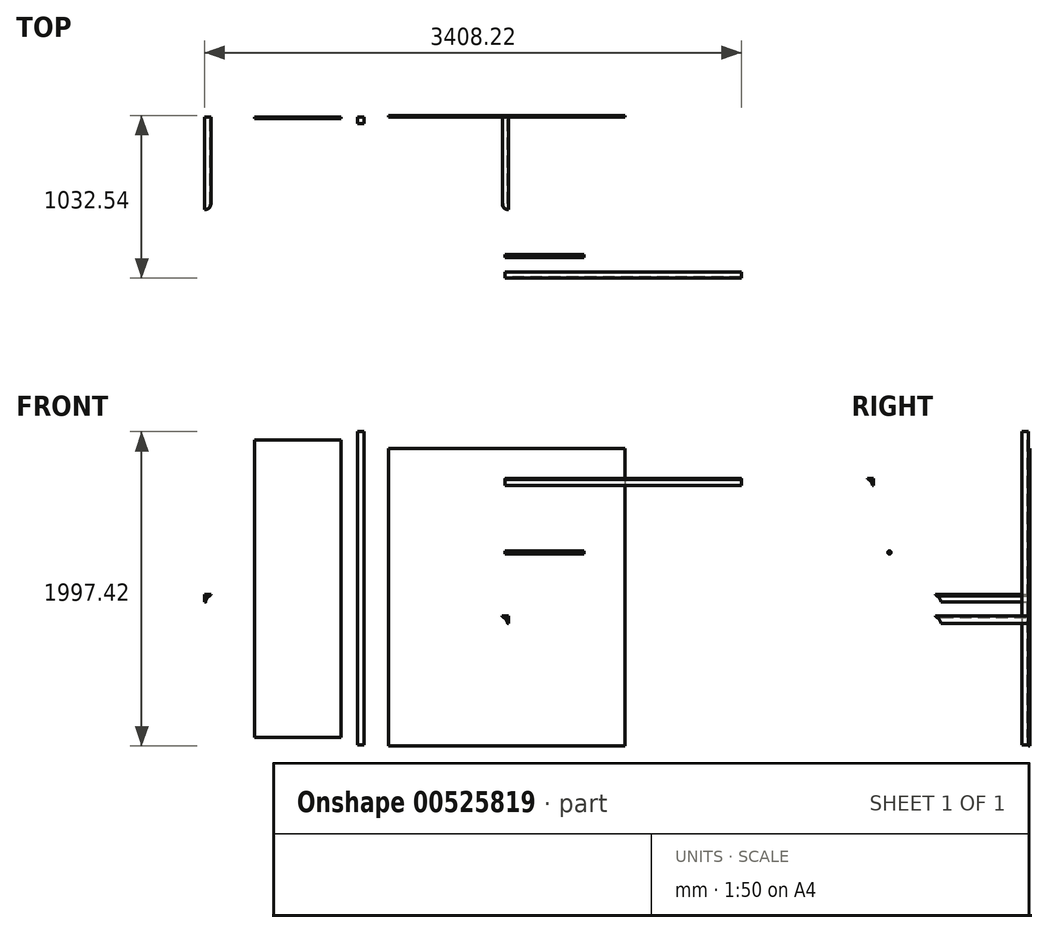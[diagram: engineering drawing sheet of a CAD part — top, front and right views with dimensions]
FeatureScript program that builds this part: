
annotation { "Feature Type Name" : "Feature", "Feature Type Description" : "" }
export const myFeature = defineFeature(function(context is Context, id is Id, definition is map)
    precondition{}
    {
        {
            var Q0;
            Q0=qCreatedBy(makeId("Front.planeOp"),FACE);
            var sketch = newSketch(context, id + "F0", { "sketchPlane" : qUnion([Q0])});
            skLineSegment(sketch, "E0.bottom", {"start": v(-740.02, 1080.66) * mm, "end": v(759.98, 1080.66) * mm});
            skLineSegment(sketch, "E0.top", {"start": v(-740.02, -809.34) * mm, "end": v(759.98, -809.34) * mm});
            skLineSegment(sketch, "E0.left", {"start": v(-740.02, 1080.66) * mm, "end": v(-740.02, -809.34) * mm});
            skLineSegment(sketch, "E0.right", {"start": v(759.98, 1080.66) * mm, "end": v(759.98, -809.34) * mm});
            skSolve(sketch);
        }
        {
            var Q0;
            Q0=makeQuery(id+"F0.imprint","IMPRINT",FACE,{"disambiguationData":[TD([[makeQuery(id+"F0.imprint","IMPRINT",EDGE,{"derivedFrom":sQuery(id+"F0.wireOp",EDGE,"E0.bottom")}),-1.0]])]});
            extrude(context, id + "F1", {"entities" : qUnion([Q0]), "depth" : 10 * mm, "offsetDistance" : 25 * mm});
        }
        {
            var Q0;
            Q0=makeQuery(id+"F1.opExtrude","CAP_FACE",FACE,{"disambiguationData":[OSD([sQuery(id+"F0.wireOp",EDGE,"E0.bottom"),sQuery(id+"F0.wireOp",EDGE,"E0.top"),sQuery(id+"F0.wireOp",EDGE,"E0.left"),sQuery(id+"F0.wireOp",EDGE,"E0.right")])],"isStart":false});
            var sketch = newSketch(context, id + "F2", { "sketchPlane" : qUnion([Q0])});
            skLineSegment(sketch, "E1.bottom", {"start": v(-937.53, 1188.08) * mm, "end": v(-897.53, 1188.08) * mm});
            skLineSegment(sketch, "E1.top", {"start": v(-937.53, -801.92) * mm, "end": v(-897.53, -801.92) * mm});
            skLineSegment(sketch, "E1.left", {"start": v(-937.53, 1188.08) * mm, "end": v(-937.53, -801.92) * mm});
            skLineSegment(sketch, "E1.right", {"start": v(-897.53, 1188.08) * mm, "end": v(-897.53, -801.92) * mm});
            skSolve(sketch);
        }
        {
            var Q0;
            Q0=makeQuery(id+"F2.imprint","IMPRINT",FACE,{"disambiguationData":[TD([[makeQuery(id+"F2.imprint","IMPRINT",EDGE,{"derivedFrom":sQuery(id+"F2.wireOp",EDGE,"E1.bottom")}),-1.0]])]});
            extrude(context, id + "F3", {"entities" : qUnion([Q0]), "depth" : 40 * mm, "offsetDistance" : 25 * mm});
        }
        {
            var Q0;
            Q0=makeQuery(id+"F1.opExtrude","CAP_FACE",FACE,{"disambiguationData":[OSD([sQuery(id+"F0.wireOp",EDGE,"E0.bottom"),sQuery(id+"F0.wireOp",EDGE,"E0.top"),sQuery(id+"F0.wireOp",EDGE,"E0.left"),sQuery(id+"F0.wireOp",EDGE,"E0.right")])],"isStart":false});
            var sketch = newSketch(context, id + "F4", { "sketchPlane" : qUnion([Q0])});
            skLineSegment(sketch, "E2.bottom", {"start": v(-1591.53, 1135.97) * mm, "end": v(-1041.53, 1135.97) * mm});
            skLineSegment(sketch, "E2.top", {"start": v(-1591.53, -754.03) * mm, "end": v(-1041.53, -754.03) * mm});
            skLineSegment(sketch, "E2.left", {"start": v(-1591.53, 1135.97) * mm, "end": v(-1591.53, -754.03) * mm});
            skLineSegment(sketch, "E2.right", {"start": v(-1041.53, 1135.97) * mm, "end": v(-1041.53, -754.03) * mm});
            skSolve(sketch);
        }
        {
            var Q0;
            Q0=makeQuery(id+"F4.imprint","IMPRINT",FACE,{"disambiguationData":[TD([[makeQuery(id+"F4.imprint","IMPRINT",EDGE,{"derivedFrom":sQuery(id+"F4.wireOp",EDGE,"E2.bottom")}),-1.0]])]});
            extrude(context, id + "F5", {"entities" : qUnion([Q0]), "depth" : 10 * mm, "offsetDistance" : 25 * mm});
        }
        {
            var Q0;
            Q0=qCreatedBy(makeId("Right.planeOp"),FACE);
            var sketch = newSketch(context, id + "F6", { "sketchPlane" : qUnion([Q0])});
            skCircle(sketch, "E3", {"center": v(-892.2, 420.17) * mm, "radius": 10 * mm});
            skSolve(sketch);
        }
        {
            var Q0;
            Q0=makeQuery(id+"F6.imprint","IMPRINT",FACE,{"disambiguationData":[TD([[makeQuery(id+"F6.imprint","IMPRINT",EDGE,{"derivedFrom":sQuery(id+"F6.wireOp",EDGE,"E3")}),1.0]])]});
            extrude(context, id + "F7", {"entities" : qUnion([Q0]), "depth" : 500 * mm, "offsetDistance" : 25 * mm});
        }
        {
            var Q0;
            Q0=makeQuery(id+"F1.opExtrude","CAP_FACE",FACE,{"disambiguationData":[OSD([sQuery(id+"F0.wireOp",EDGE,"E0.bottom"),sQuery(id+"F0.wireOp",EDGE,"E0.top"),sQuery(id+"F0.wireOp",EDGE,"E0.left"),sQuery(id+"F0.wireOp",EDGE,"E0.right")])],"isStart":false});
            var sketch = newSketch(context, id + "F8", { "sketchPlane" : qUnion([Q0])});
            skArc(sketch, "E4", {"start": v(-1875.7, 145) * mm, "mid": v(-1894.46, 128.87) * mm, "end": v(-1902.5, 105.47) * mm});
            skLineSegment(sketch, "E5", {"start": v(-1875.7, 145) * mm, "end": v(-1875.7, 149.02) * mm});
            skLineSegment(sketch, "E6", {"start": v(-1875.7, 149.02) * mm, "end": v(-1872.5, 149.02) * mm});
            skArc(sketch, "E7", {"start": v(-1872.5, 149.02) * mm, "mid": v(-1870, 150.17) * mm, "end": v(-1869.26, 152.8) * mm});
            skLineSegment(sketch, "E8", {"start": v(-1869.26, 152.8) * mm, "end": v(-1908.95, 152.8) * mm});
            skLineSegment(sketch, "E9", {"start": v(-1902.5, 105.47) * mm, "end": v(-1908.22, 105.47) * mm});
            skLineSegment(sketch, "E10", {"start": v(-1908.22, 105.47) * mm, "end": v(-1908.22, 152.8) * mm});
            skSolve(sketch);
        }
        {
            var Q0;
            Q0=makeQuery(id+"F8.imprint","IMPRINT",FACE,{"disambiguationData":[TD([[makeQuery(id+"F8.imprint","IMPRINT",EDGE,{"derivedFrom":sQuery(id+"F8.wireOp",EDGE,"E4")}),-1.0]])]});
            extrude(context, id + "F9", {"entities" : qUnion([Q0]), "depth" : 550 * mm, "offsetDistance" : 25 * mm});
        }
        {
            var Q0;
            Q0=makeQuery(id+"F9.opExtrude","CAP_FACE",FACE,{"disambiguationData":[OSD([sQuery(id+"F8.wireOp",EDGE,"E4"),sQuery(id+"F8.wireOp",EDGE,"E5"),sQuery(id+"F8.wireOp",EDGE,"E6"),sQuery(id+"F8.wireOp",EDGE,"E7"),sQuery(id+"F8.wireOp",EDGE,"E8"),sQuery(id+"F8.wireOp",EDGE,"E9"),sQuery(id+"F8.wireOp",EDGE,"E10")])],"isStart":false});
            var Q1;
            Q1=makeQuery(id+"F9.opExtrude","CAP_EDGE",EDGE,{"disambiguationData":[OSD([sQuery(id+"F8.wireOp",EDGE,"E10")])],"isStart":false});
            revolve(context, id + "F10", {"operationType" : NewBodyOperationType.ADD, "entities" : qUnion([Q0]), "axis" : qUnion([Q1]), "revolveType" : RevolveType.ONE_DIRECTION, "oppositeDirection" : true, "angle" : 90 * degree});
        }
        {
            var Q0;
            Q0=makeQuery(id+"F1.opExtrude","CAP_FACE",FACE,{"disambiguationData":[OSD([sQuery(id+"F0.wireOp",EDGE,"E0.bottom"),sQuery(id+"F0.wireOp",EDGE,"E0.top"),sQuery(id+"F0.wireOp",EDGE,"E0.left"),sQuery(id+"F0.wireOp",EDGE,"E0.right")])],"isStart":false});
            var sketch = newSketch(context, id + "F11", { "sketchPlane" : qUnion([Q0])});
            skLineSegment(sketch, "E11.MirrorCS", {"start": v(-12.22, 11.67) * mm, "end": v(-15.43, 11.67) * mm});
            skLineSegment(sketch, "E12.MirrorCS", {"start": v(-12.22, 7.63) * mm, "end": v(-12.22, 11.67) * mm});
            skArc(sketch, "E13.MirrorCS", {"start": v(-15.43, 11.67) * mm, "mid": v(-17.91, 12.8) * mm, "end": v(-18.66, 15.44) * mm});
            skLineSegment(sketch, "E14.MirrorCS", {"start": v(14.59, -31.88) * mm, "end": v(20.3, -31.88) * mm});
            skLineSegment(sketch, "E15.MirrorCS", {"start": v(-18.66, 15.44) * mm, "end": v(21.03, 15.44) * mm});
            skLineSegment(sketch, "E16.MirrorCS", {"start": v(20.3, -31.88) * mm, "end": v(20.3, 15.44) * mm});
            skArc(sketch, "E17.MirrorCS", {"start": v(-12.22, 7.63) * mm, "mid": v(6.54, -8.5) * mm, "end": v(14.59, -31.88) * mm});
            skSolve(sketch);
        }
        {
            var Q0;
            Q0=makeQuery(id+"F11.imprint","IMPRINT",FACE,{"disambiguationData":[TD([[makeQuery(id+"F11.imprint","IMPRINT",EDGE,{"derivedFrom":sQuery(id+"F11.wireOp",EDGE,"E11.MirrorCS")}),-1.0]])]});
            var Q1;
            Q1=sQuery(id+"F11.wireOp",EDGE,"E16.MirrorCS");
            var Q2;
            Q2=sQuery(id+"F11.wireOp",EDGE,"E17.MirrorCS");
            var Q3;
            Q3=sQuery(id+"F11.wireOp",EDGE,"E15.MirrorCS");
            var Q4;
            Q4=sQuery(id+"F11.wireOp",EDGE,"E16.MirrorCS");
            var Q5;
            Q5=sQuery(id+"F11.wireOp",EDGE,"E17.MirrorCS");
            var Q6;
            Q6=sQuery(id+"F11.wireOp",EDGE,"E16.MirrorCS");
            var Q7;
            Q7=sQuery(id+"F11.wireOp",EDGE,"E13.MirrorCS");
            var Q8;
            Q8=sQuery(id+"F11.wireOp",EDGE,"E12.MirrorCS");
            var Q9;
            Q9=sQuery(id+"F11.wireOp",EDGE,"E11.MirrorCS");
            var Q10;
            Q10=sQuery(id+"F11.wireOp",EDGE,"E14.MirrorCS");
            extrude(context, id + "F12", {"entities" : qUnion([Q0]), "surfaceEntities" : qUnion([Q1, Q2, Q3, Q4, Q5, Q6, Q7, Q8, Q9, Q10]), "depth" : 550 * mm, "offsetDistance" : 25 * mm});
        }
        {
            var Q0;
            Q0=makeQuery(id+"F12.opExtrude","CAP_FACE",FACE,{"disambiguationData":[OSD([sQuery(id+"F11.wireOp",EDGE,"E11.MirrorCS"),sQuery(id+"F11.wireOp",EDGE,"E12.MirrorCS"),sQuery(id+"F11.wireOp",EDGE,"E13.MirrorCS"),sQuery(id+"F11.wireOp",EDGE,"E14.MirrorCS"),sQuery(id+"F11.wireOp",EDGE,"E15.MirrorCS"),sQuery(id+"F11.wireOp",EDGE,"E17.MirrorCS"),sQuery(id+"F11.wireOp",EDGE,"E16.MirrorCS")])],"isStart":false});
            var Q1;
            Q1=makeQuery(id+"F12.opExtrude","CAP_EDGE",EDGE,{"disambiguationData":[OSD([sQuery(id+"F11.wireOp",EDGE,"E16.MirrorCS")])],"isStart":false});
            revolve(context, id + "F13", {"operationType" : NewBodyOperationType.ADD, "entities" : qUnion([Q0]), "axis" : qUnion([Q1]), "revolveType" : RevolveType.ONE_DIRECTION, "angle" : 90 * degree});
        }
        {
            var Q0;
            Q0=qCreatedBy(makeId("Right.planeOp"),FACE);
            var sketch = newSketch(context, id + "F14", { "sketchPlane" : qUnion([Q0])});
            skLineSegment(sketch, "E18.MirrorCS", {"start": v(-1026.06, 887.77) * mm, "end": v(-1029.27, 887.77) * mm});
            skLineSegment(sketch, "E19.MirrorCS", {"start": v(-1026.06, 883.73) * mm, "end": v(-1026.06, 887.77) * mm});
            skArc(sketch, "E20.MirrorCS", {"start": v(-1029.27, 887.77) * mm, "mid": v(-1031.75, 888.91) * mm, "end": v(-1032.5, 891.54) * mm});
            skLineSegment(sketch, "E21.MirrorCS", {"start": v(-999.25, 844.22) * mm, "end": v(-993.54, 844.22) * mm});
            skLineSegment(sketch, "E22.MirrorCS", {"start": v(-1032.5, 891.54) * mm, "end": v(-992.8, 891.54) * mm});
            skLineSegment(sketch, "E23.MirrorCS", {"start": v(-993.54, 844.22) * mm, "end": v(-993.54, 891.54) * mm});
            skArc(sketch, "E24.MirrorCS", {"start": v(-1026.06, 883.73) * mm, "mid": v(-1007.3, 867.61) * mm, "end": v(-999.25, 844.22) * mm});
            skSolve(sketch);
        }
        {
            var Q0;
            Q0 = qSketchRegion(id + "F14", true);
            extrude(context, id + "F15", {"entities" : qUnion([Q0]), "depth" : 1500 * mm, "offsetDistance" : 25 * mm});
        }
    });
